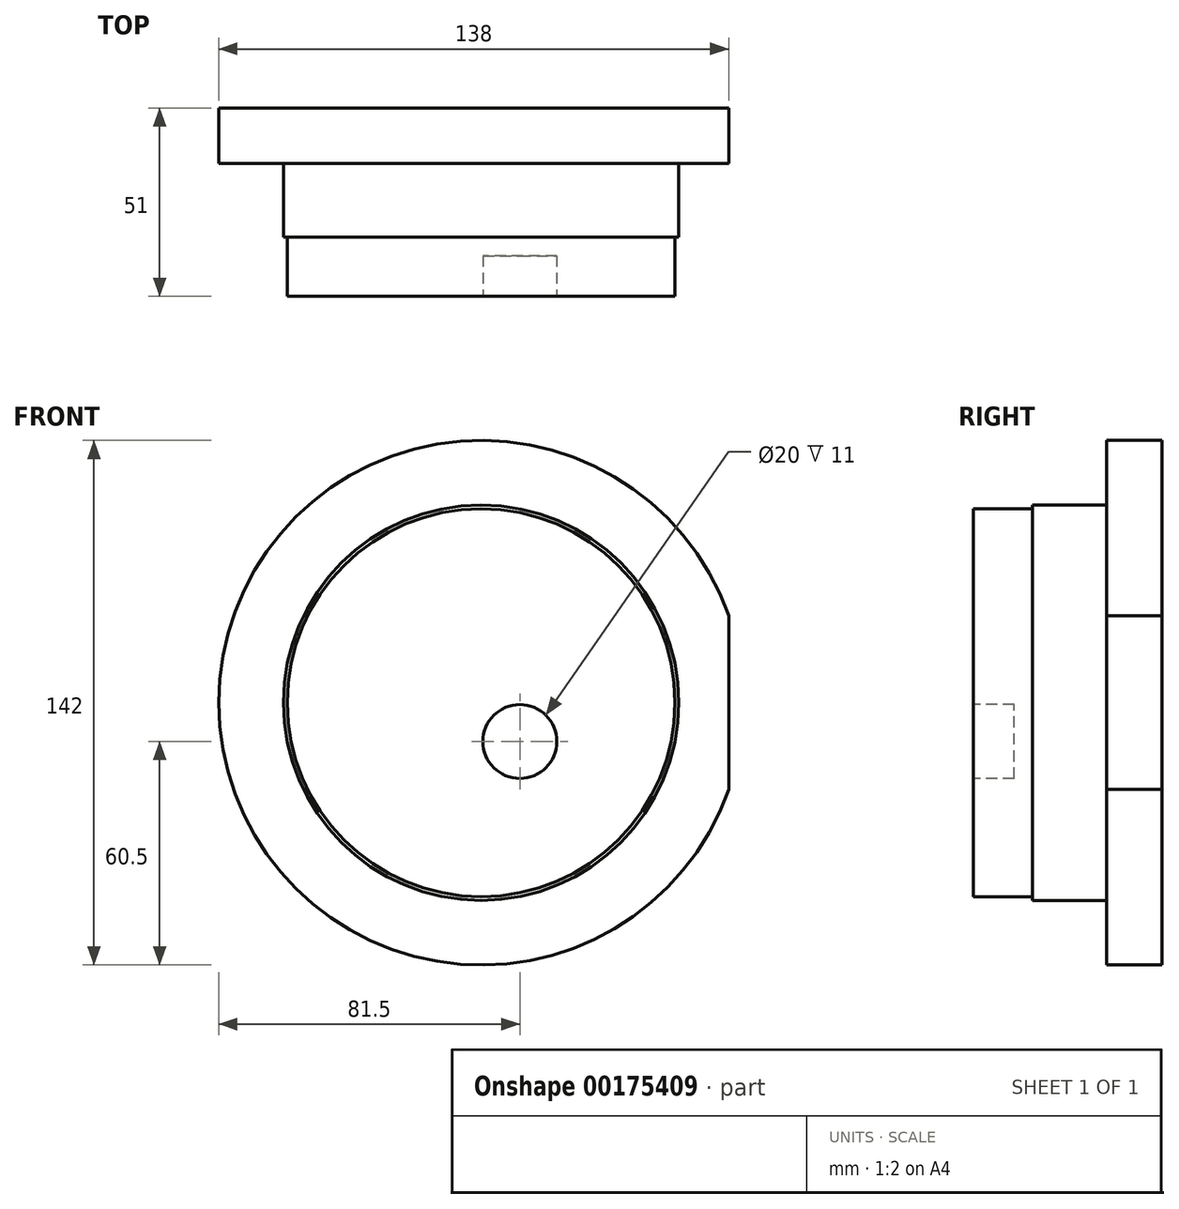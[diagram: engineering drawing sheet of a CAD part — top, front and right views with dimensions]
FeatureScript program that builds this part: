
annotation { "Feature Type Name" : "Feature", "Feature Type Description" : "" }
export const myFeature = defineFeature(function(context is Context, id is Id, definition is map)
    precondition{}
    {
        {
            var Q0;
            Q0=qCreatedBy(makeId("Front.planeOp"),FACE);
            var sketch = newSketch(context, id + "F0", { "sketchPlane" : qUnion([Q0])});
            skArc(sketch, "E0", {"start": v(67, 23.5) * mm, "mid": v(-71, 0) * mm, "end": v(67, -23.5) * mm});
            skLineSegment(sketch, "E1", {"start": v(67, 23.5) * mm, "end": v(67, -23.5) * mm});
            skSolve(sketch);
        }
        {
            var Q0;
            Q0=makeQuery(id+"F0.imprint","IMPRINT",FACE,{"disambiguationData":[TD([[makeQuery(id+"F0.imprint","IMPRINT",EDGE,{"derivedFrom":sQuery(id+"F0.wireOp",EDGE,"E0")}),1.0]])]});
            extrude(context, id + "F1", {"entities" : qUnion([Q0]), "depth" : 15 * mm});
        }
        {
            var Q0;
            Q0=makeQuery(id+"F1.opExtrude","CAP_FACE",FACE,{"disambiguationData":[OSD([sQuery(id+"F0.wireOp",EDGE,"E0"),sQuery(id+"F0.wireOp",EDGE,"E1")])],"isStart":false});
            var sketch = newSketch(context, id + "F2", { "sketchPlane" : qUnion([Q0])});
            skCircle(sketch, "E2", {"center": v(0, 0) * mm, "radius": 53.5 * mm});
            skSolve(sketch);
        }
        {
            var Q0;
            Q0=makeQuery(id+"F2.imprint","IMPRINT",FACE,{"disambiguationData":[TD([[makeQuery(id+"F2.imprint","IMPRINT",EDGE,{"derivedFrom":sQuery(id+"F2.wireOp",EDGE,"E2")}),1.0]])]});
            extrude(context, id + "F3", {"entities" : qUnion([Q0]), "operationType" : NewBodyOperationType.ADD, "depth" : 20 * mm});
        }
        {
            var Q0;
            Q0=makeQuery(id+"F3.opExtrude","CAP_FACE",FACE,{"disambiguationData":[OSD([sQuery(id+"F2.wireOp",EDGE,"E2")])],"isStart":false});
            var sketch = newSketch(context, id + "F4", { "sketchPlane" : qUnion([Q0])});
            skCircle(sketch, "E3", {"center": v(0, 0) * mm, "radius": 52.5 * mm});
            skSolve(sketch);
        }
        {
            var Q0;
            Q0=makeQuery(id+"F4.imprint","IMPRINT",FACE,{"disambiguationData":[TD([[makeQuery(id+"F4.imprint","IMPRINT",EDGE,{"derivedFrom":sQuery(id+"F4.wireOp",EDGE,"E3")}),1.0]])]});
            extrude(context, id + "F5", {"entities" : qUnion([Q0]), "operationType" : NewBodyOperationType.ADD, "depth" : 16 * mm});
        }
        {
            var Q0;
            Q0=makeQuery(id+"F5.opExtrude","CAP_FACE",FACE,{"disambiguationData":[OSD([sQuery(id+"F4.wireOp",EDGE,"E3")])],"isStart":false});
            var sketch = newSketch(context, id + "F6", { "sketchPlane" : qUnion([Q0])});
            skCircle(sketch, "E4", {"center": v(10.5, -10.5) * mm, "radius": 10 * mm});
            skSolve(sketch);
        }
        {
            var Q0;
            Q0=makeQuery(id+"F6.imprint","IMPRINT",FACE,{"disambiguationData":[TD([[makeQuery(id+"F6.imprint","IMPRINT",EDGE,{"derivedFrom":sQuery(id+"F6.wireOp",EDGE,"E4")}),1.0]])]});
            extrude(context, id + "F7", {"entities" : qUnion([Q0]), "operationType" : NewBodyOperationType.REMOVE, "oppositeDirection" : true, "depth" : 11 * mm});
        }
    });
